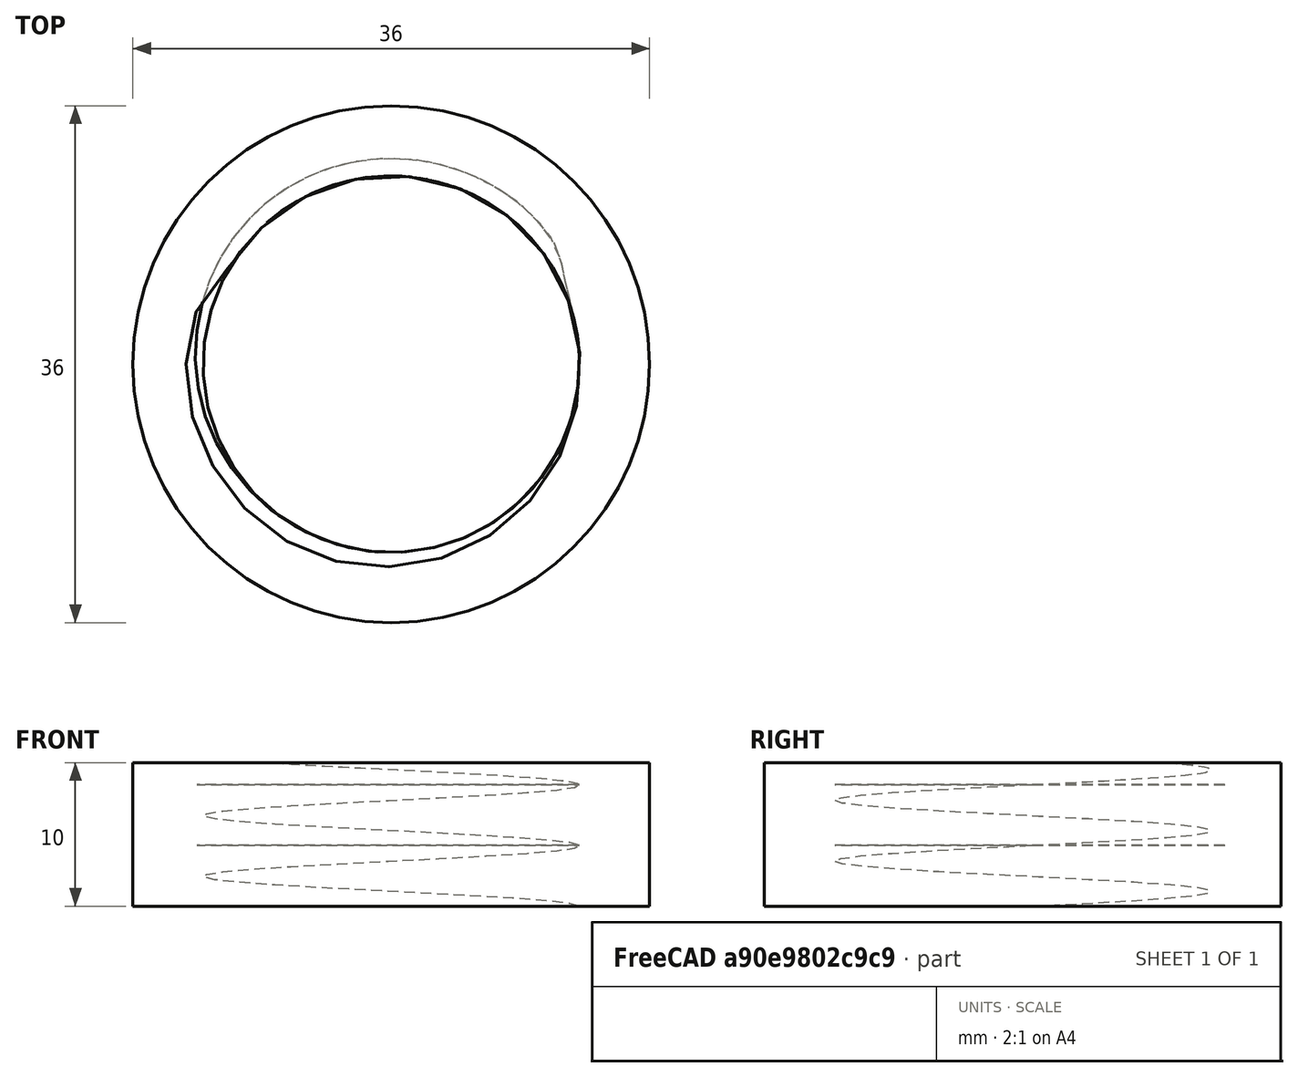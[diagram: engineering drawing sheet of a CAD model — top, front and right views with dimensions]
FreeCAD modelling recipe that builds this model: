
FCSTD DOCUMENT  (FreeCAD 0.20R29177 +426 (Git))
Label: bottle-thread-test
License: All rights reserved
LicenseURL: http://en.wikipedia.org/wiki/All_rights_reserved
objects: PartDesign::AdditiveCylinder×1, PartDesign::SubtractiveCylinder×1, Part::Part2DObjectPython×1, Part::Helix×1, PartDesign::SubtractivePipe×1, PartDesign::Body×1
note: 9 computed .brp shape members not serialized (recipe doc carries the construction recipe); baked Part::Feature solids carry a one-line shape summary decoded from their .brp

FEATURE [PartDesign::AdditiveCylinder] Cylinder
  Angle = 360
  AttacherType = Attacher::AttachEngine3D
  FirstAngle = 0
  Height = 10
  MapMode = 5
  Radius = 18
  SecondAngle = 0
  Support = -> [XY_Plane]
  expr: Radius = 36 / 2
FEATURE [PartDesign::SubtractiveCylinder] Cylinder001
  Angle = 360
  AttacherType = Attacher::AttachEngine3D
  BaseFeature = -> Cylinder
  FirstAngle = 0
  Height = 10
  Radius = 12.8
  SecondAngle = 0
  expr: Radius = 25.6 / 2
FEATURE [Part::Part2DObjectPython] Bottle_M_ThreadProfile  # Draft 2D object (typed FeaturePython)
  Area = 581.874
  Closed = true
  Continuity = C2
  Height = 11
  Helix = Helix
  Instructions = Expand this with the ... button to view instructions | Sweep this object along a helix of the same pitch to produce your thread. | It is recommended to make the helix in the ThreadProfile workbench. | If there is an active Body the ThreadProfile object will be put into it.,If not it can be dragged and dropped into the body later. | If there is an active Body when the helix is made there will be made a ShapeBinder for it | For internal threads you will need to cut the Sweep object out of a cylinder, or if using Part Design sweep it as a Subtractive Pipe. | Always use Frenet mode | I have provided some presets, but it is possible there could be some errors.  Double check for mission critical applications. | Also, the tolerances might be different from what you wish to have.  I believe the internal minor diameters are all minimum and the external are all maximum.
  InternalOrExternal = 1
  MakeFace = true
  MinorDiameter = 26.23
  Parameterization = 1
  Pitch = 4.23333
  Points = (120) [(13.0973,0.687355,0),(13.0466,1.37318,0),(12.965,2.05636,0),(12.8537,2.73605,0),(12.7134,3.4115,0),(12.5467,4.08274,0),(12.3607,4.75205,0),+113 more]
  Presets = 8
  Quality = 6
  ThreadCount = 2.59843
  Variants = 0
  Version = 1.89
  external2S_data = [-0.00461051,-0.00886426,-0.0128148,-0.0165028,-0.0199596,-0.0232105,-0.0262759,-0.0291725,-0.0319145,-0.0345137,-0.0369805,-0.0393235,-0.0415505,-0.0436681,-0.0456823,-0.0475981,-0.0494204,-0.0511532,-0.0528003,-0.0543649,-0.0558502,+698 more]
  external3S_data = [-0.00677828,-0.0128149,-0.0182584,-0.0232106,-0.0277444,-0.0319145,-0.0357632,-0.0393236,-0.0426227,-0.0456823,-0.0485208,-0.0511533,-0.0535928,-0.0558503,-0.0579353,-0.059856,-0.0616195,-0.0632319,-0.0646984,-0.0660239,-0.0672123,+698 more]
  external45_data = [-0.00137363,-0.00271738,-0.00403219,-0.00531893,-0.00657844,-0.00781148,-0.00901878,-0.010201,-0.0113589,-0.012493,-0.0136039,-0.0146921,-0.0157583,-0.0168028,-0.0178261,-0.0188288,-0.0198112,-0.0207738,-0.0217169,-0.0226409,-0.0235462,+698 more]
  external_data = [6.8683e-05,0.000137366,0.000212133,0.000297079,0.000434727,0.000654671,0.000874565,0.00109436,0.00135915,0.00172112,0.00208281,0.0024438,0.00285056,0.00336131,0.0038717,0.00438141,0.0049559,0.00562874,0.00630075,0.00697193,0.00775661,+698 more]
  internal2S_data = [0,0,0,0,0,0,0,0,0,0,0,0,0,0,0,0,0,0,0,0,0,0,0,0,0,0,0,0,0,0,0,0,0,0,0,0,0,0,0,0,0,0,0,0,0,0,0,0,0,0,0,0,0,0,0,0,0,0,0,0,0,0,0,0,0,0,0,0,0,0,0,0,0,0,0,0,0,0,0,0,0,0,0,0,0,0,0,0,0,0,0.00481128,0.00962256,0.0144338,0.0192451,0.0240564,+624 more]
  internal3S_data = [0,0,0,0,0,0,0,0,0,0,0,0,0,0,0,0,0,0,0,0,0,0,0,0,0,0,0,0,0,0,0,0,0,0,0,0,0,0,0,0,0,0,0,0,0,0,0,0,0,0,0,0,0,0,0,0,0,0,0,0,0.00721688,0.0144338,0.0216506,0.0288675,0.0360844,0.0433013,0.0505181,0.057735,0.0649519,0.0721688,0.0793857,0.0866025,+647 more]
  internal45_data = [0,0,0,0,0,0,0,0,0,0,0,0,0,0,0,0,0,0,0,0,0,0,0,0,0,0,0,0,0,0,0,0,0,0,0,0,0,0,0,0,0,0,0,0,0,0,0,0,0,0,0,0,0,0,0,0,0,0,0,0,0,0,0,0,0,0,0,0,0,0,0,0,0,0,0,0,0,0,0,0,0,0,0,0,0,0,0,0,0,0,0,0,0,0,0,0,0,0,0,0,0,0,0,0,0,0,0,0,0,0,0,0,0,0,0,0,0,0,0,0,+599 more]
  internal_data = [6.8683e-05,0.000137366,0.000212133,0.000297079,0.000434727,0.000654671,0.000874565,0.00109436,0.00135915,0.00172112,0.00208281,0.0024438,0.00285056,0.00336131,0.0038717,0.00438141,0.0049559,0.00562874,0.00630075,0.00697193,0.00775661,+698 more]
  preset_names = Bottle presets | 13-SP415(M) 2.1166666666666667 | 15-SP415(M) 2.1166666666666667 | 18-SP400(M) 3.175 | 20-SP400(M) 3.175 | 22-SP400(M) 3.175 | 24-SP400(M) 3.175 | 28-SP400(M) 4.233333333333333 | 30-SP400(M) 4.233333333333333 | 33-SP400(M) 4.233333333333333 | 35-SP400(M) 4.233333333333333 | 38-SP400(M) 4.233333333333333 | 40-SP400(M) 4.233333333333333 | 43-SP400(M) 4.233333333333333 | 45-SP400(M) 4.233333333333333 | 48-SP400(M) 4.233333333333333 | 51-SP400(M) 4.233333333333333 | 53-SP400(M) 4.233333333333333 | 58-SP400(M) 4.233333333333333 | 60-SP400(M) 4.233333333333333 | 63-SP400(M) 4.233333333333333 | 66-SP400(M) 4.233333333333333 | 70-SP400(M) 4.233333333333333 | 75-SP400(M) 4.233333333333333 | 77-SP400(M) 4.233333333333333 | 83-SP400(M) 5.08 | 89-SP400(M) 5.08 | 100-SP400(M) 5.08 | 110-SP400(M) 5.08 | 120-SP400(M) 5.08
  presets_data = [0,0,0,2.11667,11.53,11.78,2.11667,13.23,13.48,3.175,15.75,16,3.175,17.75,18,3.175,19.76,20.01,3.175,21.74,21.99,4.23333,25.25,25.5,4.23333,26.23,26.48,4.23333,29.74,29.99,4.23333,32.25,32.5,4.23333,35.1,35.35,4.23333,37.75,38,4.23333,39.62,+49 more]
FEATURE [Part::Helix] Helix
  Angle = 0
  AttacherType = Attacher::AttachEngine3D
  Height = 11
  LocalCoord = 0
  Pitch = 4.23333
  Radius = 1
  SegmentLength = 1
  Style = 0
  expr: AttachmentOffset = Bottle_M_ThreadProfile.AttachmentOffset
  expr: Height = Bottle_M_ThreadProfile.ThreadCount * Bottle_M_ThreadProfile.Pitch
  expr: MapMode = Bottle_M_ThreadProfile.MapMode
  expr: MapPathParameter = Bottle_M_ThreadProfile.MapPathParameter
  expr: MapReversed = Bottle_M_ThreadProfile.MapReversed
  expr: Pitch = Bottle_M_ThreadProfile.Pitch
  expr: SegmentLength = 1
  expr: Support = Bottle_M_ThreadProfile.Support
FEATURE [PartDesign::SubtractivePipe] SubtractivePipe
  AuxilleryCurvelinear = true
  AuxillerySpineTangent = false
  BaseFeature = -> Cylinder001
  Binormal = (0,0,0)
  Mode = 2
  Profile = -> Bottle_M_ThreadProfile
  Spine = -> Helix [Edge1,Edge2,Edge3]
  SpineTangent = false
  Transformation = 0
  Transition = 0
FEATURE [PartDesign::Body] Body
  Group = -> [Cylinder,Cylinder001,Bottle_M_ThreadProfile,Helix,SubtractivePipe]
  Origin = -> Origin
  Tip = -> SubtractivePipe
